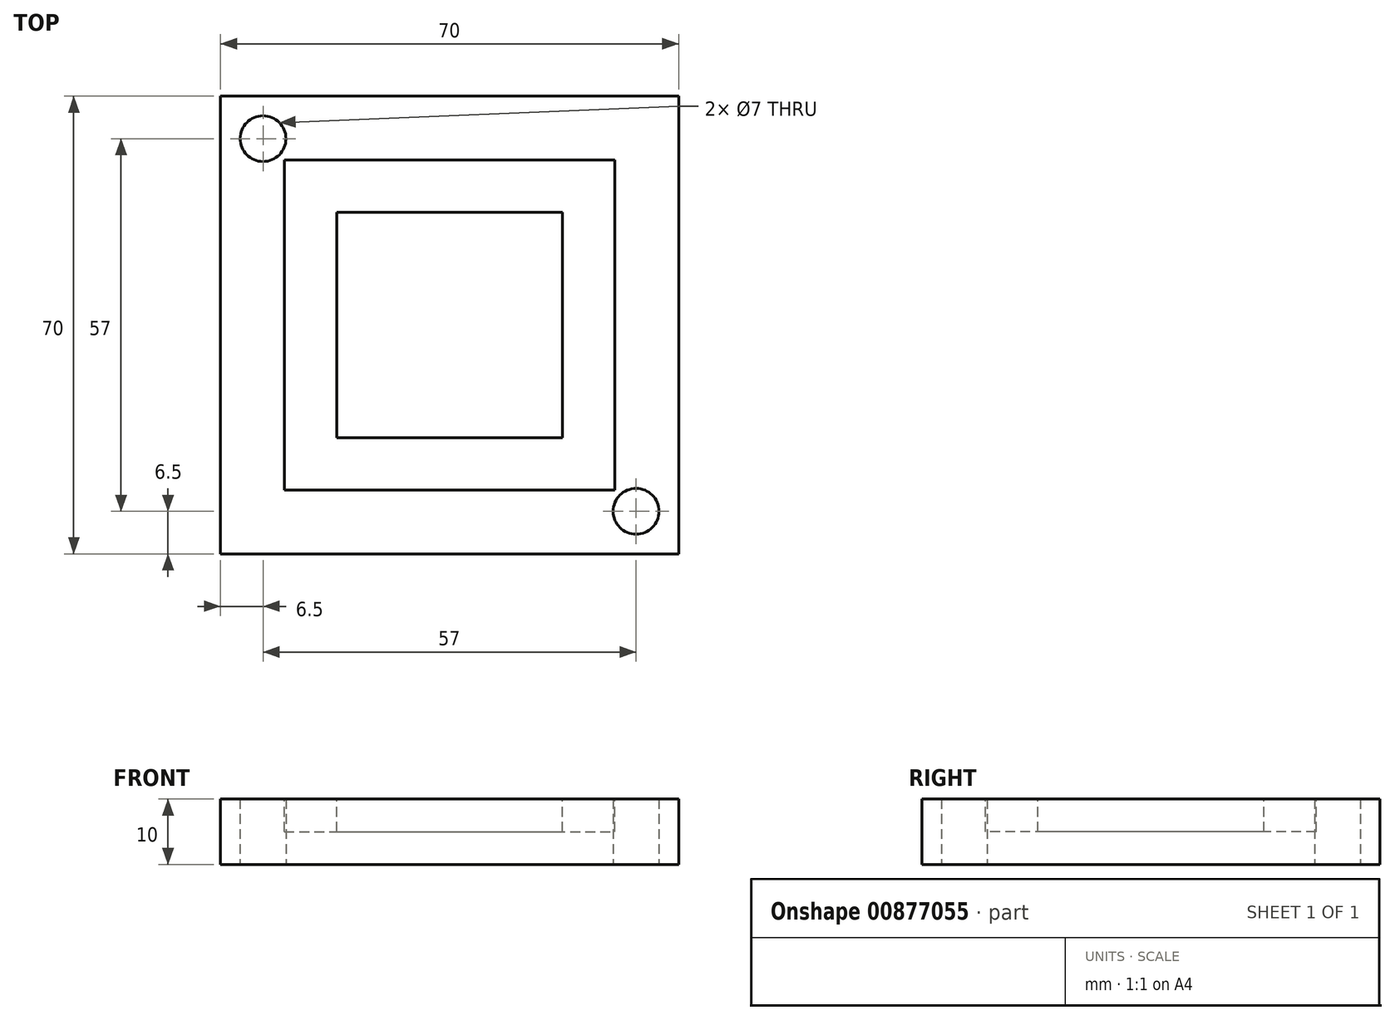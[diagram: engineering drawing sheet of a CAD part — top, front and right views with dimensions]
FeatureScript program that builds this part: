
annotation { "Feature Type Name" : "Feature", "Feature Type Description" : "" }
export const myFeature = defineFeature(function(context is Context, id is Id, definition is map)
    precondition{}
    {
        {
            var Q0;
            Q0=qCreatedBy(makeId("Top.planeOp"),FACE);
            var sketch = newSketch(context, id + "F0", { "sketchPlane" : qUnion([Q0])});
            skLineSegment(sketch, "E0.bottom", {"start": v(-35, 35) * mm, "end": v(35, 35) * mm});
            skLineSegment(sketch, "E0.top", {"start": v(-35, -35) * mm, "end": v(35, -35) * mm});
            skLineSegment(sketch, "E0.left", {"start": v(-35, 35) * mm, "end": v(-35, -35) * mm});
            skLineSegment(sketch, "E0.right", {"start": v(35, 35) * mm, "end": v(35, -35) * mm});
            skPoint(sketch, "E0.middle", {"position": v(0, 0) * mm});
            skCircle(sketch, "E1", {"center": v(-28.5, 28.5) * mm, "radius": 3.5 * mm});
            skCircle(sketch, "E2", {"center": v(28.5, -28.5) * mm, "radius": 3.5 * mm});
            skSolve(sketch);
        }
        {
            var Q0;
            Q0=makeQuery(id+"F0.imprint","IMPRINT",FACE,{"disambiguationData":[TD([[makeQuery(id+"F0.imprint","IMPRINT",EDGE,{"derivedFrom":sQuery(id+"F0.wireOp",EDGE,"E0.bottom")}),-1.0]])]});
            extrude(context, id + "F1", {"entities" : qUnion([Q0]), "depth" : 10 * mm, "offsetDistance" : 25 * mm});
        }
        {
            var Q0;
            Q0=makeQuery(id+"F1.opExtrude","CAP_FACE",FACE,{"disambiguationData":[OSD([sQuery(id+"F0.wireOp",EDGE,"E0.bottom"),sQuery(id+"F0.wireOp",EDGE,"E0.top"),sQuery(id+"F0.wireOp",EDGE,"E0.left"),sQuery(id+"F0.wireOp",EDGE,"E0.right"),sQuery(id+"F0.wireOp",EDGE,"E1"),sQuery(id+"F0.wireOp",EDGE,"E2")])],"isStart":false});
            var sketch = newSketch(context, id + "F2", { "sketchPlane" : qUnion([Q0])});
            skLineSegment(sketch, "E3.bottom", {"start": v(-25.25, 25.25) * mm, "end": v(25.25, 25.25) * mm});
            skLineSegment(sketch, "E3.top", {"start": v(-25.25, -25.25) * mm, "end": v(25.25, -25.25) * mm});
            skLineSegment(sketch, "E3.left", {"start": v(-25.25, 25.25) * mm, "end": v(-25.25, -25.25) * mm});
            skLineSegment(sketch, "E3.right", {"start": v(25.25, 25.25) * mm, "end": v(25.25, -25.25) * mm});
            skPoint(sketch, "E3.middle", {"position": v(0, 0) * mm});
            skLineSegment(sketch, "E4.bottom", {"start": v(-17.25, 17.25) * mm, "end": v(17.25, 17.25) * mm});
            skLineSegment(sketch, "E4.top", {"start": v(-17.25, -17.25) * mm, "end": v(17.25, -17.25) * mm});
            skLineSegment(sketch, "E4.left", {"start": v(-17.25, 17.25) * mm, "end": v(-17.25, -17.25) * mm});
            skLineSegment(sketch, "E4.right", {"start": v(17.25, 17.25) * mm, "end": v(17.25, -17.25) * mm});
            skSolve(sketch);
        }
        {
            var Q0;
            Q0=makeQuery(id+"F2.imprint","IMPRINT",FACE,{"disambiguationData":[TD([[makeQuery(id+"F2.imprint","IMPRINT",EDGE,{"derivedFrom":sQuery(id+"F2.wireOp",EDGE,"E3.bottom")}),-1.0]])]});
            extrude(context, id + "F3", {"entities" : qUnion([Q0]), "operationType" : NewBodyOperationType.REMOVE, "oppositeDirection" : true, "depth" : 5 * mm, "offsetDistance" : 25 * mm});
        }
    });
